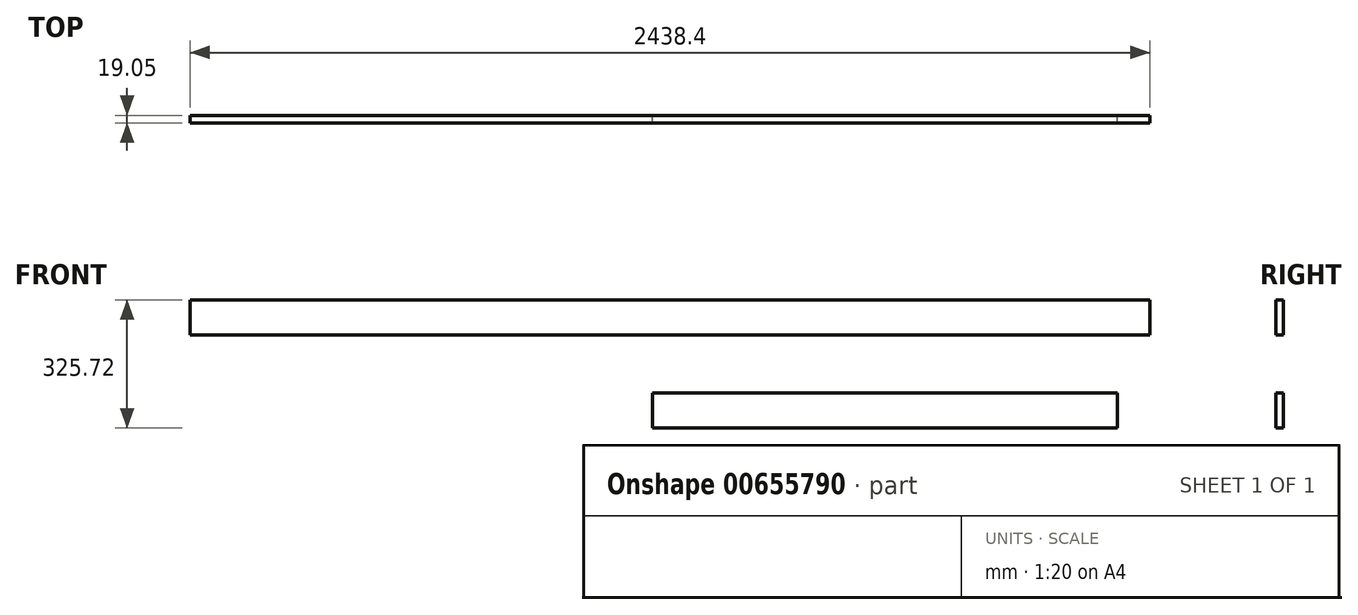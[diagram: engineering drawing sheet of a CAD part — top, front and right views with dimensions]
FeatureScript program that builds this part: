
annotation { "Feature Type Name" : "Feature", "Feature Type Description" : "" }
export const myFeature = defineFeature(function(context is Context, id is Id, definition is map)
    precondition{}
    {
        {
            var Q0;
            Q0=qCreatedBy(makeId("Front.planeOp"),FACE);
            var sketch = newSketch(context, id + "F0", { "sketchPlane" : qUnion([Q0])});
            skLineSegment(sketch, "E0.bottom", {"start": v(1219.2, 44.45) * mm, "end": v(-1219.2, 44.45) * mm});
            skLineSegment(sketch, "E0.top", {"start": v(1219.2, -44.45) * mm, "end": v(-1219.2, -44.45) * mm});
            skLineSegment(sketch, "E0.left", {"start": v(1219.2, 44.45) * mm, "end": v(1219.2, -44.45) * mm});
            skLineSegment(sketch, "E0.right", {"start": v(-1219.2, 44.45) * mm, "end": v(-1219.2, -44.45) * mm});
            skPoint(sketch, "E0.middle", {"position": v(0, 0) * mm});
            skLineSegment(sketch, "E1.bottom", {"start": v(-44.69, -192.37) * mm, "end": v(1136.41, -192.37) * mm});
            skLineSegment(sketch, "E1.top", {"start": v(-44.69, -281.27) * mm, "end": v(1136.41, -281.27) * mm});
            skLineSegment(sketch, "E1.left", {"start": v(-44.69, -192.37) * mm, "end": v(-44.69, -281.27) * mm});
            skLineSegment(sketch, "E1.right", {"start": v(1136.41, -192.37) * mm, "end": v(1136.41, -281.27) * mm});
            skSolve(sketch);
        }
        {
            var Q0;
            Q0=makeQuery(id+"F0.imprint","IMPRINT",FACE,{"disambiguationData":[TD([[makeQuery(id+"F0.imprint","IMPRINT",EDGE,{"derivedFrom":sQuery(id+"F0.wireOp",EDGE,"E0.bottom")}),1.0]])]});
            extrude(context, id + "F1", {"entities" : qUnion([Q0]), "depth" : 19.05 * mm, "offsetDistance" : 25.4 * mm});
        }
        {
            var Q0;
            Q0=makeQuery(id+"F1.opExtrude","SWEPT_BODY",BODY,{"disambiguationData":[OSD([sQuery(id+"F0.wireOp",EDGE,"E0.bottom"),sQuery(id+"F0.wireOp",EDGE,"E0.top"),sQuery(id+"F0.wireOp",EDGE,"E0.left"),sQuery(id+"F0.wireOp",EDGE,"E0.right")])]});
            transform(context, id + "F2", {"entities" : qUnion([Q0]), "transformType" : TransformType.TRANSLATION_3D, "dx" : 0 * mm, "dy" : 0 * mm, "dz" : 0 * mm, "makeCopy" : true});
        }
        {
            var Q0;
            Q0=makeQuery(id+"F0.imprint","IMPRINT",FACE,{"disambiguationData":[TD([[makeQuery(id+"F0.imprint","IMPRINT",EDGE,{"derivedFrom":sQuery(id+"F0.wireOp",EDGE,"E1.bottom")}),-1.0]])]});
            extrude(context, id + "F3", {"entities" : qUnion([Q0]), "depth" : 19.05 * mm, "offsetDistance" : 25.4 * mm});
        }
    });
